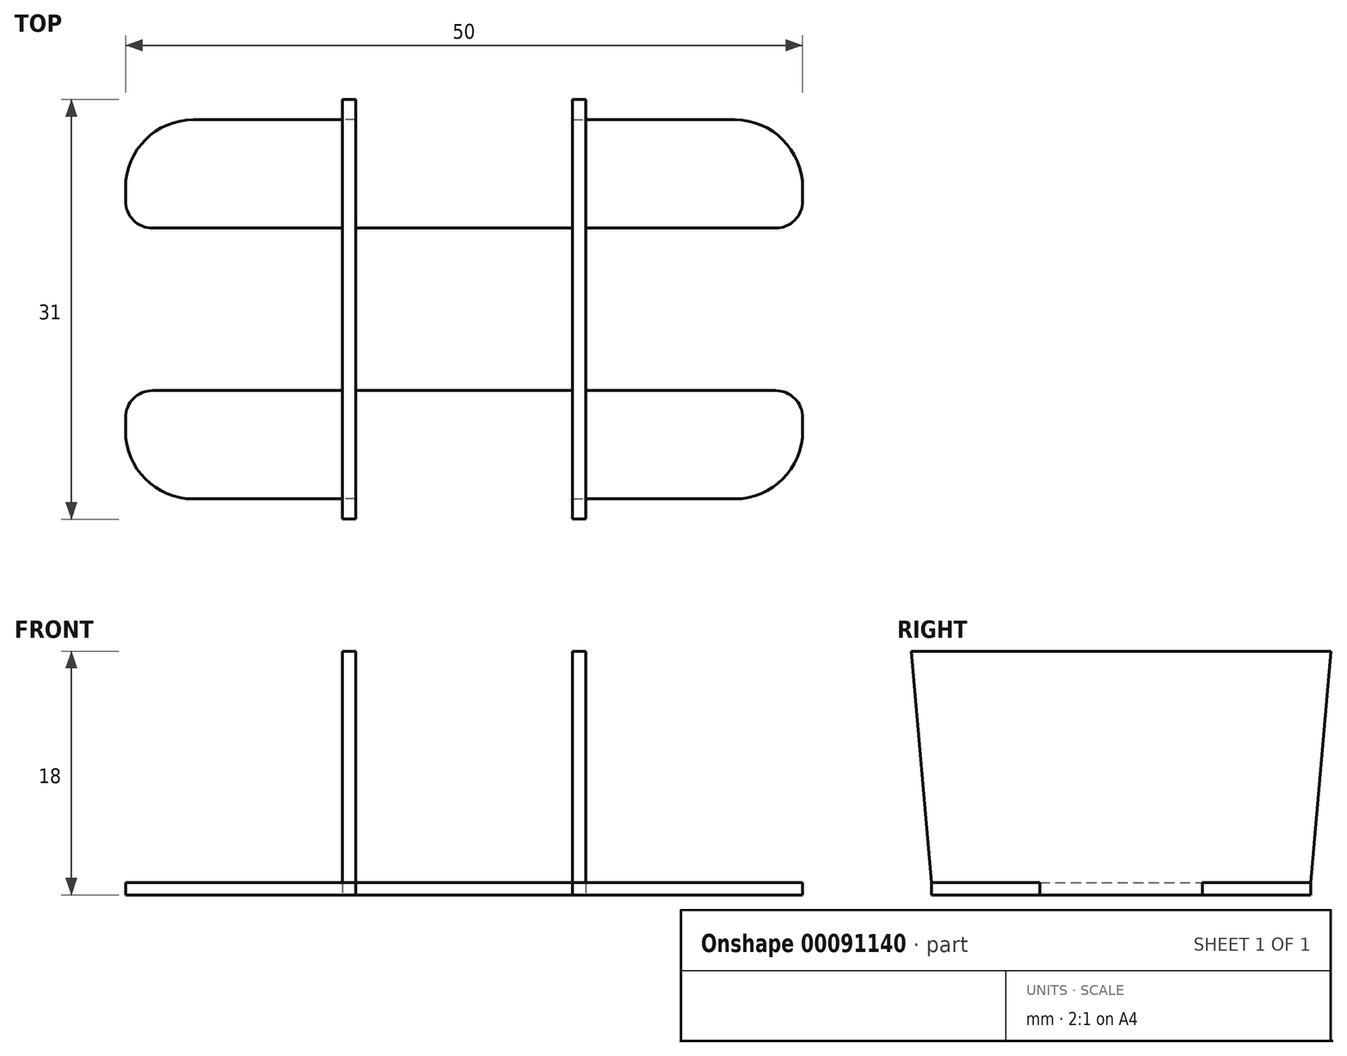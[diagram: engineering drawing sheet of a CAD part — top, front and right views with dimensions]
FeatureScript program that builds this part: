
annotation { "Feature Type Name" : "Feature", "Feature Type Description" : "" }
export const myFeature = defineFeature(function(context is Context, id is Id, definition is map)
    precondition{}
    {
        {
            var Q0;
            Q0=qCreatedBy(makeId("Top.planeOp"),FACE);
            var sketch = newSketch(context, id + "F0", { "sketchPlane" : qUnion([Q0])});
            skLineSegment(sketch, "E0.bottom", {"start": v(-20, 14) * mm, "end": v(20, 14) * mm});
            skLineSegment(sketch, "E0.top", {"start": v(-20, -14) * mm, "end": v(20, -14) * mm});
            skLineSegment(sketch, "E0.left", {"start": v(-25, 9) * mm, "end": v(-25, -9) * mm});
            skLineSegment(sketch, "E0.right", {"start": v(25, 9) * mm, "end": v(25, -9) * mm});
            skPoint(sketch, "E0.middle", {"position": v(0, 0) * mm});
            skLineSegment(sketch, "E1", {"start": v(-25, 6) * mm, "end": v(25, 6) * mm});
            skLineSegment(sketch, "E2", {"start": v(25, -6) * mm, "end": v(-25, -6) * mm});
            skLineSegment(sketch, "E3", {"start": v(-9, 14) * mm, "end": v(-9, -14) * mm});
            skLineSegment(sketch, "E4", {"start": v(9, -14) * mm, "end": v(9, 14) * mm});
            skPoint(sketch, "E5.visualSharp", {"position": v(-25, 14) * mm});
            skArc(sketch, "E5.filletArc", {"start": v(-20, 14) * mm, "mid": v(-23.54, 12.54) * mm, "end": v(-25, 9) * mm});
            skPoint(sketch, "E6.visualSharp", {"position": v(-25, -14) * mm});
            skArc(sketch, "E6.filletArc", {"start": v(-25, -9) * mm, "mid": v(-23.54, -12.54) * mm, "end": v(-20, -14) * mm});
            skPoint(sketch, "E7.visualSharp", {"position": v(25, -14) * mm});
            skArc(sketch, "E7.filletArc", {"start": v(20, -14) * mm, "mid": v(23.54, -12.54) * mm, "end": v(25, -9) * mm});
            skPoint(sketch, "E8.visualSharp", {"position": v(25, 14) * mm});
            skArc(sketch, "E8.filletArc", {"start": v(25, 9) * mm, "mid": v(23.54, 12.54) * mm, "end": v(20, 14) * mm});
            skLineSegment(sketch, "E9", {"start": v(-8, 14) * mm, "end": v(-8, -14) * mm});
            skLineSegment(sketch, "E10", {"start": v(8, -14) * mm, "end": v(8, 14) * mm});
            skSolve(sketch);
        }
        {
            var Q0;
            {var subQ5=sQuery(id+"F0.wireOp",EDGE,"E5.filletArc");Q0=makeQuery(id+"F0.imprint","IMPRINT",FACE,{"disambiguationData":[TD([[makeQuery(id+"F0.imprint","IMPRINT",EDGE,{"derivedFrom":subQ5}),1.0]])]});}
            var Q1;
            {var subQ0=sQuery(id+"F0.wireOp",EDGE,"E3");var subQ1=sQuery(id+"F0.wireOp",EDGE,"E0.bottom");var subQ2=makeQuery(id+"F0.imprint","INTERSECT",VERTEX,{"derivedFrom":[subQ1,subQ0]});Q1=makeQuery(id+"F0.imprint","IMPRINT",FACE,{"disambiguationData":[TD([[makeQuery(id+"F0.imprint","IMPRINT",EDGE,{"disambiguationData":[TD([[subQ2,-1.0]])],"derivedFrom":subQ1}),-1.0]])]});}
            var Q2;
            {var subQ0=sQuery(id+"F0.wireOp",EDGE,"E3");var subQ1=sQuery(id+"F0.wireOp",EDGE,"E1");var subQ2=makeQuery(id+"F0.imprint","INTERSECT",VERTEX,{"derivedFrom":[subQ1,subQ0]});Q2=makeQuery(id+"F0.imprint","IMPRINT",FACE,{"disambiguationData":[TD([[makeQuery(id+"F0.imprint","IMPRINT",EDGE,{"disambiguationData":[TD([[subQ2,-1.0]])],"derivedFrom":subQ1}),-1.0]])]});}
            var Q3;
            {var subQ0=sQuery(id+"F0.wireOp",EDGE,"E3");var subQ1=sQuery(id+"F0.wireOp",EDGE,"E0.top");var subQ2=makeQuery(id+"F0.imprint","INTERSECT",VERTEX,{"derivedFrom":[subQ1,subQ0]});Q3=makeQuery(id+"F0.imprint","IMPRINT",FACE,{"disambiguationData":[TD([[makeQuery(id+"F0.imprint","IMPRINT",EDGE,{"disambiguationData":[TD([[subQ2,-1.0]])],"derivedFrom":subQ1}),1.0]])]});}
            var Q4;
            {var subQ7=sQuery(id+"F0.wireOp",EDGE,"E6.filletArc");Q4=makeQuery(id+"F0.imprint","IMPRINT",FACE,{"disambiguationData":[TD([[makeQuery(id+"F0.imprint","IMPRINT",EDGE,{"derivedFrom":subQ7}),1.0]])]});}
            var Q5;
            {var subQ7=sQuery(id+"F0.wireOp",EDGE,"E7.filletArc");Q5=makeQuery(id+"F0.imprint","IMPRINT",FACE,{"disambiguationData":[TD([[makeQuery(id+"F0.imprint","IMPRINT",EDGE,{"derivedFrom":subQ7}),1.0]])]});}
            var Q6;
            {var subQ5=sQuery(id+"F0.wireOp",EDGE,"E8.filletArc");Q6=makeQuery(id+"F0.imprint","IMPRINT",FACE,{"disambiguationData":[TD([[makeQuery(id+"F0.imprint","IMPRINT",EDGE,{"derivedFrom":subQ5}),1.0]])]});}
            var Q7;
            {var subQ0=sQuery(id+"F0.wireOp",EDGE,"E4");var subQ1=sQuery(id+"F0.wireOp",EDGE,"E0.bottom");var subQ2=makeQuery(id+"F0.imprint","INTERSECT",VERTEX,{"derivedFrom":[subQ1,subQ0]});Q7=makeQuery(id+"F0.imprint","IMPRINT",FACE,{"disambiguationData":[TD([[makeQuery(id+"F0.imprint","IMPRINT",EDGE,{"disambiguationData":[TD([[subQ2,1.0]])],"derivedFrom":subQ1}),-1.0]])]});}
            var Q8;
            {var subQ0=sQuery(id+"F0.wireOp",EDGE,"E10");var subQ1=sQuery(id+"F0.wireOp",EDGE,"E1");var subQ2=makeQuery(id+"F0.imprint","INTERSECT",VERTEX,{"derivedFrom":[subQ1,subQ0]});Q8=makeQuery(id+"F0.imprint","IMPRINT",FACE,{"disambiguationData":[TD([[makeQuery(id+"F0.imprint","IMPRINT",EDGE,{"disambiguationData":[TD([[subQ2,-1.0]])],"derivedFrom":subQ1}),-1.0]])]});}
            var Q9;
            {var subQ0=sQuery(id+"F0.wireOp",EDGE,"E4");var subQ1=sQuery(id+"F0.wireOp",EDGE,"E0.top");var subQ2=makeQuery(id+"F0.imprint","INTERSECT",VERTEX,{"derivedFrom":[subQ1,subQ0]});Q9=makeQuery(id+"F0.imprint","IMPRINT",FACE,{"disambiguationData":[TD([[makeQuery(id+"F0.imprint","IMPRINT",EDGE,{"disambiguationData":[TD([[subQ2,1.0]])],"derivedFrom":subQ1}),1.0]])]});}
            var Q10;
            {var subQ0=sQuery(id+"F0.wireOp",EDGE,"E9");var subQ1=sQuery(id+"F0.wireOp",EDGE,"E1");var subQ2=makeQuery(id+"F0.imprint","INTERSECT",VERTEX,{"derivedFrom":[subQ1,subQ0]});Q10=makeQuery(id+"F0.imprint","IMPRINT",FACE,{"disambiguationData":[TD([[makeQuery(id+"F0.imprint","IMPRINT",EDGE,{"disambiguationData":[TD([[subQ2,-1.0]])],"derivedFrom":subQ1}),-1.0]])]});}
            extrude(context, id + "F1", {"entities" : qUnion([Q0, Q1, Q2, Q3, Q4, Q5, Q6, Q7, Q8, Q9, Q10]), "depth" : .9 * mm});
        }
        {
            var Q0;
            {var subQ0=sQuery(id+"F0.wireOp",EDGE,"E3");var subQ1=sQuery(id+"F0.wireOp",EDGE,"E0.top");var subQ2=makeQuery(id+"F0.imprint","INTERSECT",VERTEX,{"derivedFrom":[subQ1,subQ0]});Q0=makeQuery(id+"F0.imprint","IMPRINT",FACE,{"disambiguationData":[TD([[makeQuery(id+"F0.imprint","IMPRINT",EDGE,{"disambiguationData":[TD([[subQ2,-1.0]])],"derivedFrom":subQ1}),1.0]])]});}
            var Q1;
            {var subQ0=sQuery(id+"F0.wireOp",EDGE,"E3");var subQ1=sQuery(id+"F0.wireOp",EDGE,"E1");var subQ2=makeQuery(id+"F0.imprint","INTERSECT",VERTEX,{"derivedFrom":[subQ1,subQ0]});Q1=makeQuery(id+"F0.imprint","IMPRINT",FACE,{"disambiguationData":[TD([[makeQuery(id+"F0.imprint","IMPRINT",EDGE,{"disambiguationData":[TD([[subQ2,-1.0]])],"derivedFrom":subQ1}),-1.0]])]});}
            var Q2;
            {var subQ0=sQuery(id+"F0.wireOp",EDGE,"E3");var subQ1=sQuery(id+"F0.wireOp",EDGE,"E0.bottom");var subQ2=makeQuery(id+"F0.imprint","INTERSECT",VERTEX,{"derivedFrom":[subQ1,subQ0]});Q2=makeQuery(id+"F0.imprint","IMPRINT",FACE,{"disambiguationData":[TD([[makeQuery(id+"F0.imprint","IMPRINT",EDGE,{"disambiguationData":[TD([[subQ2,-1.0]])],"derivedFrom":subQ1}),-1.0]])]});}
            var Q3;
            {var subQ0=sQuery(id+"F0.wireOp",EDGE,"E4");var subQ1=sQuery(id+"F0.wireOp",EDGE,"E0.bottom");var subQ2=makeQuery(id+"F0.imprint","INTERSECT",VERTEX,{"derivedFrom":[subQ1,subQ0]});Q3=makeQuery(id+"F0.imprint","IMPRINT",FACE,{"disambiguationData":[TD([[makeQuery(id+"F0.imprint","IMPRINT",EDGE,{"disambiguationData":[TD([[subQ2,1.0]])],"derivedFrom":subQ1}),-1.0]])]});}
            var Q4;
            {var subQ0=sQuery(id+"F0.wireOp",EDGE,"E10");var subQ1=sQuery(id+"F0.wireOp",EDGE,"E1");var subQ2=makeQuery(id+"F0.imprint","INTERSECT",VERTEX,{"derivedFrom":[subQ1,subQ0]});Q4=makeQuery(id+"F0.imprint","IMPRINT",FACE,{"disambiguationData":[TD([[makeQuery(id+"F0.imprint","IMPRINT",EDGE,{"disambiguationData":[TD([[subQ2,-1.0]])],"derivedFrom":subQ1}),-1.0]])]});}
            var Q5;
            {var subQ0=sQuery(id+"F0.wireOp",EDGE,"E4");var subQ1=sQuery(id+"F0.wireOp",EDGE,"E0.top");var subQ2=makeQuery(id+"F0.imprint","INTERSECT",VERTEX,{"derivedFrom":[subQ1,subQ0]});Q5=makeQuery(id+"F0.imprint","IMPRINT",FACE,{"disambiguationData":[TD([[makeQuery(id+"F0.imprint","IMPRINT",EDGE,{"disambiguationData":[TD([[subQ2,1.0]])],"derivedFrom":subQ1}),1.0]])]});}
            extrude(context, id + "F2", {"entities" : qUnion([Q0, Q1, Q2, Q3, Q4, Q5]), "operationType" : NewBodyOperationType.ADD, "depth" : 18 * mm});
        }
        {
            var Q0;
            Q0=makeQuery(id+"F1.opExtrude","SWEPT_EDGE",EDGE,{"disambiguationData":[OSD([sQuery(id+"F0.wireOp",EDGE,"E0.left"),sQuery(id+"F0.wireOp",EDGE,"E1")])]});
            var Q1;
            Q1=makeQuery(id+"F1.opExtrude","SWEPT_EDGE",EDGE,{"disambiguationData":[OSD([sQuery(id+"F0.wireOp",EDGE,"E1"),sQuery(id+"F0.wireOp",EDGE,"E3")])]});
            var Q2;
            Q2=makeQuery(id+"F1.opExtrude","SWEPT_EDGE",EDGE,{"disambiguationData":[OSD([sQuery(id+"F0.wireOp",EDGE,"E2"),sQuery(id+"F0.wireOp",EDGE,"E3")])]});
            var Q3;
            Q3=makeQuery(id+"F1.opExtrude","SWEPT_EDGE",EDGE,{"disambiguationData":[OSD([sQuery(id+"F0.wireOp",EDGE,"E0.left"),sQuery(id+"F0.wireOp",EDGE,"E2")])]});
            var Q4;
            Q4=makeQuery(id+"F1.opExtrude","SWEPT_EDGE",EDGE,{"disambiguationData":[OSD([sQuery(id+"F0.wireOp",EDGE,"E1"),sQuery(id+"F0.wireOp",EDGE,"E9")])]});
            var Q5;
            Q5=makeQuery(id+"F1.opExtrude","SWEPT_EDGE",EDGE,{"disambiguationData":[OSD([sQuery(id+"F0.wireOp",EDGE,"E1"),sQuery(id+"F0.wireOp",EDGE,"E10")])]});
            var Q6;
            Q6=makeQuery(id+"F1.opExtrude","SWEPT_EDGE",EDGE,{"disambiguationData":[OSD([sQuery(id+"F0.wireOp",EDGE,"E0.right"),sQuery(id+"F0.wireOp",EDGE,"E1")])]});
            var Q7;
            Q7=makeQuery(id+"F1.opExtrude","SWEPT_EDGE",EDGE,{"disambiguationData":[OSD([sQuery(id+"F0.wireOp",EDGE,"E0.right"),sQuery(id+"F0.wireOp",EDGE,"E2")])]});
            var Q8;
            Q8=makeQuery(id+"F1.opExtrude","SWEPT_EDGE",EDGE,{"disambiguationData":[OSD([sQuery(id+"F0.wireOp",EDGE,"E1"),sQuery(id+"F0.wireOp",EDGE,"E4")])]});
            var Q9;
            Q9=makeQuery(id+"F1.opExtrude","SWEPT_EDGE",EDGE,{"disambiguationData":[OSD([sQuery(id+"F0.wireOp",EDGE,"E2"),sQuery(id+"F0.wireOp",EDGE,"E4")])]});
            var Q10;
            Q10=makeQuery(id+"F1.opExtrude","SWEPT_EDGE",EDGE,{"disambiguationData":[OSD([sQuery(id+"F0.wireOp",EDGE,"E2"),sQuery(id+"F0.wireOp",EDGE,"E10")])]});
            var Q11;
            Q11=makeQuery(id+"F1.opExtrude","SWEPT_EDGE",EDGE,{"disambiguationData":[OSD([sQuery(id+"F0.wireOp",EDGE,"E2"),sQuery(id+"F0.wireOp",EDGE,"E9")])]});
            fillet(context, id + "F3", {"entities" : qUnion([Q0, Q1, Q2, Q3, Q4, Q5, Q6, Q7, Q8, Q9, Q10, Q11]), "radius" : 2 * mm, "tangentPropagation" : true, "allowEdgeOverflow" : false});
        }
        {
            var Q0;
            {var subQ0=sQuery(id+"F0.wireOp",EDGE,"E4");Q0=makeQuery(id+"F2.boolean.opBoolean","MERGE",FACE,{"derivedFrom":[makeQuery(id+"F1.opExtrude","SWEPT_FACE",FACE,{"disambiguationData":[OSD([subQ0])]}),makeQuery(id+"F2.opExtrude","SWEPT_FACE",FACE,{"disambiguationData":[OSD([subQ0])]})]});}
            var sketch = newSketch(context, id + "F4", { "sketchPlane" : qUnion([Q0])});
            skLineSegment(sketch, "E11", {"start": v(-14, 0.9) * mm, "end": v(-15.5, 18) * mm});
            skLineSegment(sketch, "E12", {"start": v(-15.5, 18) * mm, "end": v(-14, 18) * mm});
            skLineSegment(sketch, "E13", {"start": v(-14, 18) * mm, "end": v(-14, 0.9) * mm});
            skLineSegment(sketch, "E14", {"start": v(14, 18) * mm, "end": v(15.5, 18) * mm});
            skLineSegment(sketch, "E15", {"start": v(15.5, 18) * mm, "end": v(14, 0.9) * mm});
            skLineSegment(sketch, "E16", {"start": v(14, 0.9) * mm, "end": v(14, 18) * mm});
            skSolve(sketch);
        }
        {
            var Q0;
            Q0=qSketchRegion(id+"F4",true);
            extrude(context, id + "F5", {"entities" : qUnion([Q0]), "operationType" : NewBodyOperationType.ADD, "oppositeDirection" : true, "depth" : 1 * mm});
        }
        {
            var Q0;
            {var subQ0=sQuery(id+"F0.wireOp",EDGE,"E3");Q0=makeQuery(id+"F2.boolean.opBoolean","MERGE",FACE,{"derivedFrom":[makeQuery(id+"F1.opExtrude","SWEPT_FACE",FACE,{"disambiguationData":[OSD([subQ0])]}),makeQuery(id+"F2.opExtrude","SWEPT_FACE",FACE,{"disambiguationData":[OSD([subQ0])]})]});}
            var sketch = newSketch(context, id + "F6", { "sketchPlane" : qUnion([Q0])});
            skLineSegment(sketch, "E17", {"start": v(-14, 18) * mm, "end": v(-15.5, 18) * mm});
            skLineSegment(sketch, "E18", {"start": v(-15.5, 18) * mm, "end": v(-14, 0.9) * mm});
            skLineSegment(sketch, "E19", {"start": v(-14, 0.9) * mm, "end": v(-14, 18) * mm});
            skLineSegment(sketch, "E20", {"start": v(14, 18) * mm, "end": v(15.5, 18) * mm});
            skLineSegment(sketch, "E21", {"start": v(15.5, 18) * mm, "end": v(14, 0.9) * mm});
            skLineSegment(sketch, "E22", {"start": v(14, 0.9) * mm, "end": v(14, 18) * mm});
            skSolve(sketch);
        }
        {
            var Q0;
            Q0=qSketchRegion(id+"F6",true);
            extrude(context, id + "F7", {"entities" : qUnion([Q0]), "operationType" : NewBodyOperationType.ADD, "oppositeDirection" : true, "depth" : 1 * mm});
        }
    });
